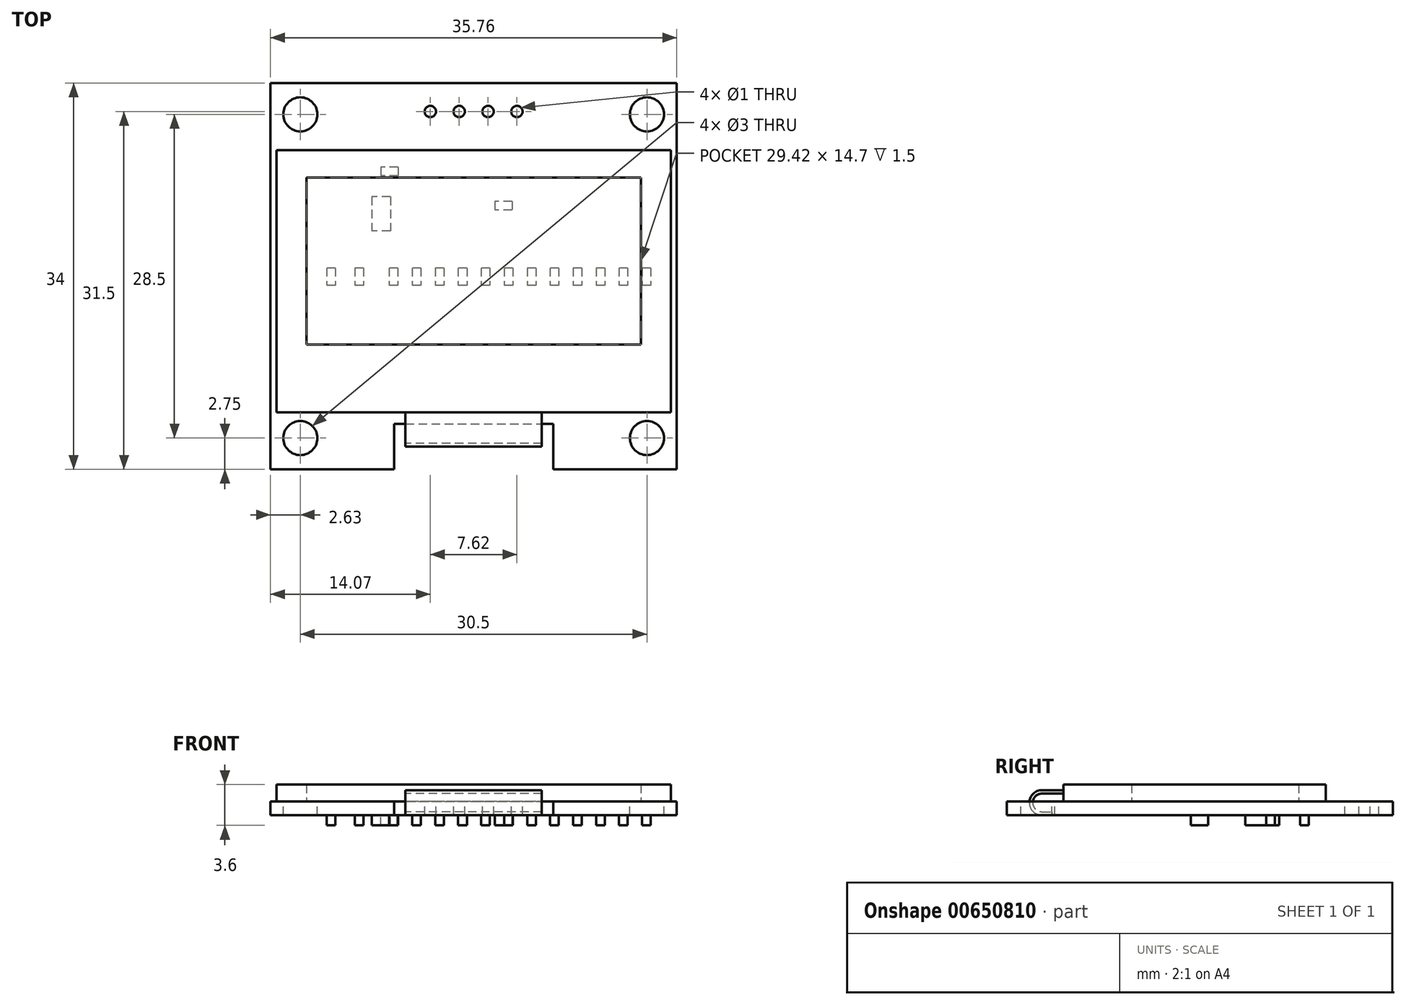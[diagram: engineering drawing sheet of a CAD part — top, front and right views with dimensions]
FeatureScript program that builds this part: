
annotation { "Feature Type Name" : "Feature", "Feature Type Description" : "" }
export const myFeature = defineFeature(function(context is Context, id is Id, definition is map)
    precondition{}
    {
        {
            var Q0;
            Q0=qCreatedBy(makeId("Top.planeOp"),FACE);
            var sketch = newSketch(context, id + "F0", { "sketchPlane" : qUnion([Q0])});
            skLineSegment(sketch, "E0.bottom", {"start": v(17.88, 34) * mm, "end": v(-17.88, 34) * mm});
            skLineSegment(sketch, "E0.top", {"start": v(17.88, 0) * mm, "end": v(7, 0) * mm});
            skLineSegment(sketch, "E0.left", {"start": v(17.88, 34) * mm, "end": v(17.88, 0) * mm});
            skLineSegment(sketch, "E0.right", {"start": v(-17.88, 34) * mm, "end": v(-17.88, 0) * mm});
            skPoint(sketch, "E0.middle", {"position": v(0, 17) * mm});
            skLineSegment(sketch, "E1", {"start": v(-7, 4) * mm, "end": v(7, 4) * mm});
            skPoint(sketch, "E2", {"position": v(0, 4) * mm});
            skLineSegment(sketch, "E3", {"start": v(7, 4) * mm, "end": v(7, 0) * mm});
            skLineSegment(sketch, "E4", {"start": v(-7, 4) * mm, "end": v(-7, 0) * mm});
            skLineSegment(sketch, "E5.trimOffspring", {"start": v(-7, 0) * mm, "end": v(-17.88, 0) * mm});
            skLineSegment(sketch, "E6.bottom", {"start": v(-15.25, 31.25) * mm, "end": v(15.25, 31.25) * mm, "construction": true});
            skLineSegment(sketch, "E6.top", {"start": v(-15.25, 2.75) * mm, "end": v(15.25, 2.75) * mm, "construction": true});
            skLineSegment(sketch, "E6.left", {"start": v(-15.25, 31.25) * mm, "end": v(-15.25, 2.75) * mm, "construction": true});
            skLineSegment(sketch, "E6.right", {"start": v(15.25, 31.25) * mm, "end": v(15.25, 2.75) * mm, "construction": true});
            skCircle(sketch, "E7", {"center": v(-15.25, 2.75) * mm, "radius": 1.5 * mm});
            skCircle(sketch, "E8", {"center": v(-15.25, 31.25) * mm, "radius": 1.5 * mm});
            skCircle(sketch, "E9", {"center": v(15.25, 31.25) * mm, "radius": 1.5 * mm});
            skCircle(sketch, "E10", {"center": v(15.25, 2.75) * mm, "radius": 1.5 * mm});
            skCircle(sketch, "E11", {"center": v(3.8, 31.5) * mm, "radius": 0.5 * mm});
            skCircle(sketch, "E12.1.0.0", {"center": v(1.27, 31.5) * mm, "radius": 0.5 * mm});
            skCircle(sketch, "E12.2.0.0", {"center": v(-1.27, 31.5) * mm, "radius": 0.5 * mm});
            skCircle(sketch, "E12.3.0.0", {"center": v(-3.81, 31.5) * mm, "radius": 0.5 * mm});
            skLineSegment(sketch, "E12.direction1", {"start": v(3.8, 31.5) * mm, "end": v(1.27, 31.5) * mm, "construction": true});
            skSolve(sketch);
        }
        {
            var Q0;
            Q0=makeQuery(id+"F0.imprint","IMPRINT",FACE,{"disambiguationData":[TD([[makeQuery(id+"F0.imprint","IMPRINT",EDGE,{"derivedFrom":sQuery(id+"F0.wireOp",EDGE,"E0.bottom")}),1.0]])]});
            extrude(context, id + "F1", {"entities" : qUnion([Q0]), "oppositeDirection" : true, "depth" : 1.2 * mm, "offsetDistance" : 25 * mm});
        }
        {
            var Q0;
            Q0=qCreatedBy(makeId("Top.planeOp"),FACE);
            var sketch = newSketch(context, id + "F2", { "sketchPlane" : qUnion([Q0])});
            skLineSegment(sketch, "E13.bottom", {"start": v(-17.35, 28.1) * mm, "end": v(17.35, 28.1) * mm});
            skLineSegment(sketch, "E13.top", {"start": v(-17.35, 5) * mm, "end": v(17.35, 5) * mm});
            skLineSegment(sketch, "E13.left", {"start": v(-17.35, 28.1) * mm, "end": v(-17.35, 5) * mm});
            skLineSegment(sketch, "E13.right", {"start": v(17.35, 28.1) * mm, "end": v(17.35, 5) * mm});
            skPoint(sketch, "E13.middle", {"position": v(0, 16.55) * mm});
            skLineSegment(sketch, "E14.bottom", {"start": v(14.7, 25.7) * mm, "end": v(-14.71, 25.7) * mm});
            skLineSegment(sketch, "E14.top", {"start": v(14.7, 11) * mm, "end": v(-14.71, 11) * mm});
            skLineSegment(sketch, "E14.left", {"start": v(14.7, 25.7) * mm, "end": v(14.7, 11) * mm});
            skLineSegment(sketch, "E14.right", {"start": v(-14.71, 25.7) * mm, "end": v(-14.71, 11) * mm});
            skPoint(sketch, "E14.middle", {"position": v(0, 18.35) * mm});
            skSolve(sketch);
        }
        {
            var Q0;
            Q0=makeQuery(id+"F2.imprint","IMPRINT",FACE,{"disambiguationData":[TD([[makeQuery(id+"F2.imprint","IMPRINT",EDGE,{"derivedFrom":sQuery(id+"F2.wireOp",EDGE,"E13.bottom")}),-1.0]])]});
            extrude(context, id + "F3", {"entities" : qUnion([Q0]), "depth" : 1.5 * mm, "offsetDistance" : 25 * mm});
        }
        {
            var Q0;
            Q0=makeQuery(id+"F2.imprint","IMPRINT",FACE,{"disambiguationData":[TD([[makeQuery(id+"F2.imprint","IMPRINT",EDGE,{"derivedFrom":sQuery(id+"F2.wireOp",EDGE,"E14.bottom")}),1.0]])]});
            var Q1;
            Q1=makeQuery(id+"F3.opExtrude","CAP_FACE",FACE,{"disambiguationData":[OSD([sQuery(id+"F2.wireOp",EDGE,"E13.bottom"),sQuery(id+"F2.wireOp",EDGE,"E13.top"),sQuery(id+"F2.wireOp",EDGE,"E13.left"),sQuery(id+"F2.wireOp",EDGE,"E13.right"),sQuery(id+"F2.wireOp",EDGE,"E14.bottom"),sQuery(id+"F2.wireOp",EDGE,"E14.top"),sQuery(id+"F2.wireOp",EDGE,"E14.left"),sQuery(id+"F2.wireOp",EDGE,"E14.right")])],"isStart":false});
            extrude(context, id + "F4", {"entities" : qUnion([Q0]), "endBound" : BoundingType.UP_TO_SURFACE, "depth" : 25 * mm, "endBoundEntityFace" : qUnion([Q1]), "offsetDistance" : 25 * mm});
        }
        {
            var Q0;
            Q0=qCreatedBy(makeId("Right.planeOp"),FACE);
            var sketch = newSketch(context, id + "F5", { "sketchPlane" : qUnion([Q0])});
            skArc(sketch, "E15", {"start": v(3.1, 1) * mm, "mid": v(2, -0.1) * mm, "end": v(3.1, -1.2) * mm});
            skLineSegment(sketch, "E16", {"start": v(3.1, -1.2) * mm, "end": v(4, -1.2) * mm});
            skLineSegment(sketch, "E17", {"start": v(3.1, 1) * mm, "end": v(5, 1) * mm});
            skLineSegment(sketch, "E18", {"start": v(5, 1) * mm, "end": v(5, 0.7) * mm});
            skLineSegment(sketch, "E19", {"start": v(4, -0.9) * mm, "end": v(4, -1.2) * mm});
            skArc(sketch, "E20", {"start": v(3.1, -0.9) * mm, "mid": v(2.3, -0.1) * mm, "end": v(3.1, 0.7) * mm});
            skLineSegment(sketch, "E21", {"start": v(3.1, 0.7) * mm, "end": v(5, 0.7) * mm});
            skLineSegment(sketch, "E22", {"start": v(3.1, -0.9) * mm, "end": v(4, -0.9) * mm});
            skSolve(sketch);
        }
        {
            var Q0;
            Q0=makeQuery(id+"F5.imprint","IMPRINT",FACE,{"disambiguationData":[TD([[makeQuery(id+"F5.imprint","IMPRINT",EDGE,{"derivedFrom":sQuery(id+"F5.wireOp",EDGE,"E15")}),1.0]])]});
            extrude(context, id + "F6", {"entities" : qUnion([Q0]), "operationType" : NewBodyOperationType.ADD, "depth" : 12 * mm, "offsetDistance" : 25 * mm, "symmetric" : true});
        }
        {
            var Q0;
            Q0=makeQuery(id+"F1.opExtrude","CAP_FACE",FACE,{"disambiguationData":[OSD([sQuery(id+"F0.wireOp",EDGE,"E0.bottom"),sQuery(id+"F0.wireOp",EDGE,"E0.top"),sQuery(id+"F0.wireOp",EDGE,"E0.left"),sQuery(id+"F0.wireOp",EDGE,"E0.right"),sQuery(id+"F0.wireOp",EDGE,"E1"),sQuery(id+"F0.wireOp",EDGE,"E3"),sQuery(id+"F0.wireOp",EDGE,"E4"),sQuery(id+"F0.wireOp",EDGE,"E5.trimOffspring"),sQuery(id+"F0.wireOp",EDGE,"E7"),sQuery(id+"F0.wireOp",EDGE,"E8"),sQuery(id+"F0.wireOp",EDGE,"E9"),sQuery(id+"F0.wireOp",EDGE,"E10"),sQuery(id+"F0.wireOp",EDGE,"E11"),sQuery(id+"F0.wireOp",EDGE,"E12.1.0.0"),sQuery(id+"F0.wireOp",EDGE,"E12.2.0.0"),sQuery(id+"F0.wireOp",EDGE,"E12.3.0.0")])],"isStart":false});
            var sketch = newSketch(context, id + "F7", { "sketchPlane" : qUnion([Q0])});
            skLineSegment(sketch, "E23.bottom", {"start": v(15.57, -17.72) * mm, "end": v(14.81, -17.72) * mm});
            skLineSegment(sketch, "E23.top", {"start": v(15.57, -16.2) * mm, "end": v(14.81, -16.2) * mm});
            skLineSegment(sketch, "E23.left", {"start": v(15.57, -17.72) * mm, "end": v(15.57, -16.2) * mm});
            skLineSegment(sketch, "E23.right", {"start": v(14.81, -17.72) * mm, "end": v(14.81, -16.2) * mm});
            skLineSegment(sketch, "E24.1.0.0", {"start": v(12.8, -17.72) * mm, "end": v(12.8, -16.2) * mm});
            skLineSegment(sketch, "E24.1.0.1", {"start": v(13.55, -17.72) * mm, "end": v(12.8, -17.72) * mm});
            skLineSegment(sketch, "E24.1.0.2", {"start": v(13.55, -17.72) * mm, "end": v(13.55, -16.2) * mm});
            skLineSegment(sketch, "E24.1.0.3", {"start": v(13.55, -16.2) * mm, "end": v(12.8, -16.2) * mm});
            skLineSegment(sketch, "E24.2.0.0", {"start": v(10.77, -17.72) * mm, "end": v(10.77, -16.2) * mm});
            skLineSegment(sketch, "E24.2.0.1", {"start": v(11.53, -17.72) * mm, "end": v(10.77, -17.72) * mm});
            skLineSegment(sketch, "E24.2.0.2", {"start": v(11.53, -17.72) * mm, "end": v(11.53, -16.2) * mm});
            skLineSegment(sketch, "E24.2.0.3", {"start": v(11.53, -16.2) * mm, "end": v(10.77, -16.2) * mm});
            skLineSegment(sketch, "E24.3.0.0", {"start": v(8.75, -17.72) * mm, "end": v(8.75, -16.2) * mm});
            skLineSegment(sketch, "E24.3.0.1", {"start": v(9.51, -17.72) * mm, "end": v(8.75, -17.72) * mm});
            skLineSegment(sketch, "E24.3.0.2", {"start": v(9.51, -17.72) * mm, "end": v(9.51, -16.2) * mm});
            skLineSegment(sketch, "E24.3.0.3", {"start": v(9.51, -16.2) * mm, "end": v(8.75, -16.2) * mm});
            skLineSegment(sketch, "E24.4.0.0", {"start": v(6.73, -17.72) * mm, "end": v(6.73, -16.2) * mm});
            skLineSegment(sketch, "E24.4.0.1", {"start": v(7.49, -17.72) * mm, "end": v(6.73, -17.72) * mm});
            skLineSegment(sketch, "E24.4.0.2", {"start": v(7.49, -17.72) * mm, "end": v(7.49, -16.2) * mm});
            skLineSegment(sketch, "E24.4.0.3", {"start": v(7.49, -16.2) * mm, "end": v(6.73, -16.2) * mm});
            skLineSegment(sketch, "E24.5.0.0", {"start": v(4.7, -17.72) * mm, "end": v(4.7, -16.2) * mm});
            skLineSegment(sketch, "E24.5.0.1", {"start": v(5.47, -17.72) * mm, "end": v(4.7, -17.72) * mm});
            skLineSegment(sketch, "E24.5.0.2", {"start": v(5.47, -17.72) * mm, "end": v(5.47, -16.2) * mm});
            skLineSegment(sketch, "E24.5.0.3", {"start": v(5.47, -16.2) * mm, "end": v(4.7, -16.2) * mm});
            skLineSegment(sketch, "E24.6.0.0", {"start": v(2.68, -17.72) * mm, "end": v(2.68, -16.2) * mm});
            skLineSegment(sketch, "E24.6.0.1", {"start": v(3.45, -17.72) * mm, "end": v(2.68, -17.72) * mm});
            skLineSegment(sketch, "E24.6.0.2", {"start": v(3.45, -17.72) * mm, "end": v(3.45, -16.2) * mm});
            skLineSegment(sketch, "E24.6.0.3", {"start": v(3.45, -16.2) * mm, "end": v(2.68, -16.2) * mm});
            skLineSegment(sketch, "E24.7.0.0", {"start": v(0.66, -17.72) * mm, "end": v(0.66, -16.2) * mm});
            skLineSegment(sketch, "E24.7.0.1", {"start": v(1.42, -17.72) * mm, "end": v(0.66, -17.72) * mm});
            skLineSegment(sketch, "E24.7.0.2", {"start": v(1.42, -17.72) * mm, "end": v(1.42, -16.2) * mm});
            skLineSegment(sketch, "E24.7.0.3", {"start": v(1.42, -16.2) * mm, "end": v(0.66, -16.2) * mm});
            skLineSegment(sketch, "E24.8.0.0", {"start": v(-1.36, -17.72) * mm, "end": v(-1.36, -16.2) * mm});
            skLineSegment(sketch, "E24.8.0.1", {"start": v(-0.6, -17.72) * mm, "end": v(-1.36, -17.72) * mm});
            skLineSegment(sketch, "E24.8.0.2", {"start": v(-0.6, -17.72) * mm, "end": v(-0.6, -16.2) * mm});
            skLineSegment(sketch, "E24.8.0.3", {"start": v(-0.6, -16.2) * mm, "end": v(-1.36, -16.2) * mm});
            skLineSegment(sketch, "E24.9.0.0", {"start": v(-3.38, -17.72) * mm, "end": v(-3.38, -16.2) * mm});
            skLineSegment(sketch, "E24.9.0.1", {"start": v(-2.62, -17.72) * mm, "end": v(-3.38, -17.72) * mm});
            skLineSegment(sketch, "E24.9.0.2", {"start": v(-2.62, -17.72) * mm, "end": v(-2.62, -16.2) * mm});
            skLineSegment(sketch, "E24.9.0.3", {"start": v(-2.62, -16.2) * mm, "end": v(-3.38, -16.2) * mm});
            skLineSegment(sketch, "E24.10.0.0", {"start": v(-5.4, -17.72) * mm, "end": v(-5.4, -16.2) * mm});
            skLineSegment(sketch, "E24.10.0.1", {"start": v(-4.64, -17.72) * mm, "end": v(-5.4, -17.72) * mm});
            skLineSegment(sketch, "E24.10.0.2", {"start": v(-4.64, -17.72) * mm, "end": v(-4.64, -16.2) * mm});
            skLineSegment(sketch, "E24.10.0.3", {"start": v(-4.64, -16.2) * mm, "end": v(-5.4, -16.2) * mm});
            skLineSegment(sketch, "E24.11.0.0", {"start": v(-7.42, -17.72) * mm, "end": v(-7.43, -16.2) * mm});
            skLineSegment(sketch, "E24.11.0.1", {"start": v(-6.66, -17.72) * mm, "end": v(-7.42, -17.72) * mm});
            skLineSegment(sketch, "E24.11.0.2", {"start": v(-6.66, -17.72) * mm, "end": v(-6.66, -16.2) * mm});
            skLineSegment(sketch, "E24.11.0.3", {"start": v(-6.66, -16.2) * mm, "end": v(-7.43, -16.2) * mm});
            skLineSegment(sketch, "E24.direction1", {"start": v(14.81, -17.72) * mm, "end": v(12.8, -17.72) * mm, "construction": true});
            skLineSegment(sketch, "E25.bottom", {"start": v(-9.7, -17.72) * mm, "end": v(-10.46, -17.72) * mm});
            skLineSegment(sketch, "E25.top", {"start": v(-9.7, -16.2) * mm, "end": v(-10.46, -16.2) * mm});
            skLineSegment(sketch, "E25.left", {"start": v(-9.7, -17.72) * mm, "end": v(-9.7, -16.2) * mm});
            skLineSegment(sketch, "E25.right", {"start": v(-10.46, -17.72) * mm, "end": v(-10.46, -16.2) * mm});
            skLineSegment(sketch, "E26.bottom", {"start": v(-12.16, -17.72) * mm, "end": v(-12.92, -17.72) * mm});
            skLineSegment(sketch, "E26.top", {"start": v(-12.16, -16.2) * mm, "end": v(-12.92, -16.2) * mm});
            skLineSegment(sketch, "E26.left", {"start": v(-12.16, -17.72) * mm, "end": v(-12.16, -16.2) * mm});
            skLineSegment(sketch, "E26.right", {"start": v(-12.92, -17.72) * mm, "end": v(-12.92, -16.2) * mm});
            skLineSegment(sketch, "E27.bottom", {"start": v(-7.33, -24) * mm, "end": v(-8.98, -24) * mm});
            skLineSegment(sketch, "E27.top", {"start": v(-7.33, -21) * mm, "end": v(-8.98, -21) * mm});
            skLineSegment(sketch, "E27.left", {"start": v(-7.33, -24) * mm, "end": v(-7.33, -21) * mm});
            skLineSegment(sketch, "E27.right", {"start": v(-8.98, -24) * mm, "end": v(-8.98, -21) * mm});
            skLineSegment(sketch, "E28.bottom", {"start": v(-6.65, -26.6) * mm, "end": v(-8.18, -26.6) * mm});
            skLineSegment(sketch, "E28.top", {"start": v(-6.65, -25.84) * mm, "end": v(-8.18, -25.84) * mm});
            skLineSegment(sketch, "E28.left", {"start": v(-6.65, -26.6) * mm, "end": v(-6.65, -25.84) * mm});
            skLineSegment(sketch, "E28.right", {"start": v(-8.18, -26.6) * mm, "end": v(-8.18, -25.84) * mm});
            skLineSegment(sketch, "E29.bottom", {"start": v(3.37, -23.6) * mm, "end": v(1.85, -23.6) * mm});
            skLineSegment(sketch, "E29.top", {"start": v(3.37, -22.84) * mm, "end": v(1.85, -22.84) * mm});
            skLineSegment(sketch, "E29.left", {"start": v(3.37, -23.6) * mm, "end": v(3.37, -22.84) * mm});
            skLineSegment(sketch, "E29.right", {"start": v(1.85, -23.6) * mm, "end": v(1.85, -22.84) * mm});
            skSolve(sketch);
        }
        {
            var Q0;
            Q0 = qSketchRegion(id + "F7", true);
            extrude(context, id + "F8", {"entities" : qUnion([Q0]), "operationType" : NewBodyOperationType.ADD, "depth" : 0.9 * mm, "offsetDistance" : 25 * mm});
        }
    });
